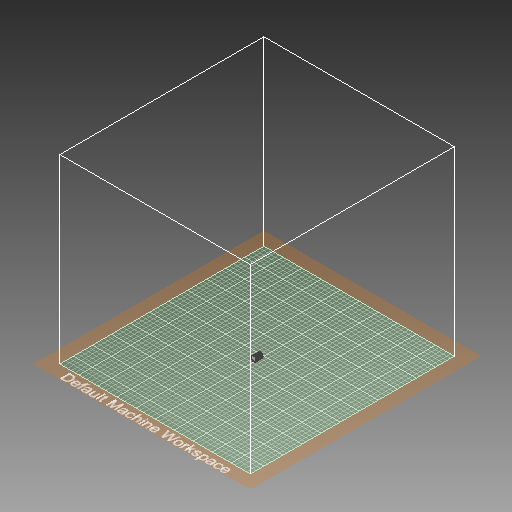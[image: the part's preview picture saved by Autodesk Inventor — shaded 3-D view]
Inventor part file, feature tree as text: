
AUTODESK INVENTOR PART (.ipt)
format: ipt  version: 2019.3 (Build 233278000, 278)  size: 1,231,872 bytes
history: native  units: mm
features: extrude x1
ambient origin geometry x8: Origin, YZ Plane, XZ Plane, XY Plane, X Axis, Y Axis, Z Axis, Center Point
bodies: Body1 (feature_tree)
feature tree (1):
  extrude  "Extrusion2"  Depth=5.047545mm
